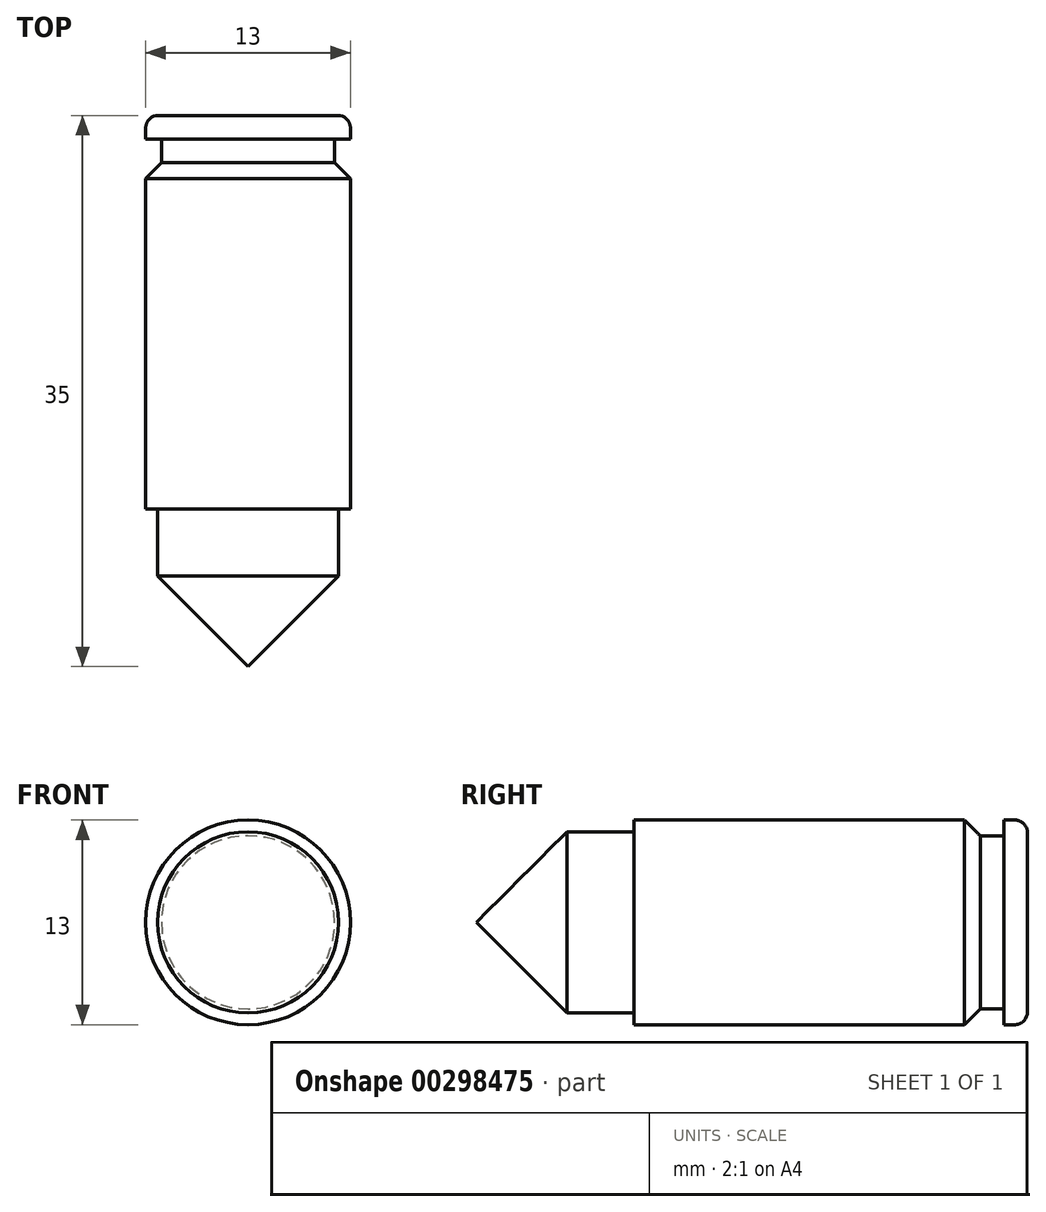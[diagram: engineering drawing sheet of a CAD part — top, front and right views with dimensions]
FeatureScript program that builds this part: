
annotation { "Feature Type Name" : "Feature", "Feature Type Description" : "" }
export const myFeature = defineFeature(function(context is Context, id is Id, definition is map)
    precondition{}
    {
        {
            var Q0;
            Q0=qCreatedBy(makeId("Front.planeOp"),FACE);
            var sketch = newSketch(context, id + "F0", { "sketchPlane" : qUnion([Q0])});
            skCircle(sketch, "E0", {"center": v(0, 0) * mm, "radius": 5.75 * mm});
            skSolve(sketch);
        }
        {
            var Q0;
            Q0 = qSketchRegion(id + "F0", true);
            extrude(context, id + "F1", {"entities" : qUnion([Q0]), "depth" : 10 * mm});
        }
        {
            var Q0;
            Q0=makeQuery(id+"F1.opExtrude","CAP_EDGE",EDGE,{"disambiguationData":[OSD([sQuery(id+"F0.wireOp",EDGE,"E0")])],"isStart":false});
            chamfer(context, id + "F2", {"entities" : qUnion([Q0]), "width" : 5.75 * mm, "tangentPropagation" : true});
        }
        {
            var Q0;
            Q0=makeQuery(id+"F1.opExtrude","CAP_FACE",FACE,{"disambiguationData":[OSD([sQuery(id+"F0.wireOp",EDGE,"E0")])],"isStart":true});
            var sketch = newSketch(context, id + "F3", { "sketchPlane" : qUnion([Q0])});
            skCircle(sketch, "E1", {"center": v(0, 0) * mm, "radius": 6.5 * mm});
            skSolve(sketch);
        }
        {
            var Q0;
            Q0 = qSketchRegion(id + "F3", true);
            extrude(context, id + "F4", {"entities" : qUnion([Q0]), "operationType" : NewBodyOperationType.ADD, "depth" : 22 * mm});
        }
        {
            var Q0;
            Q0=makeQuery(id+"F4.opExtrude","CAP_EDGE",EDGE,{"disambiguationData":[OSD([sQuery(id+"F3.wireOp",EDGE,"E1")])],"isStart":false});
            chamfer(context, id + "F5", {"entities" : qUnion([Q0]), "width" : 1 * mm, "tangentPropagation" : true});
        }
        {
            var Q0;
            Q0=makeQuery(id+"F4.opExtrude","CAP_FACE",FACE,{"disambiguationData":[OSD([sQuery(id+"F3.wireOp",EDGE,"E1")])],"isStart":false});
            var sketch = newSketch(context, id + "F6", { "sketchPlane" : qUnion([Q0])});
            skCircle(sketch, "E2", {"center": v(0, 0) * mm, "radius": 5.5 * mm});
            skSolve(sketch);
        }
        {
            var Q0;
            Q0 = qSketchRegion(id + "F6", true);
            extrude(context, id + "F7", {"entities" : qUnion([Q0]), "operationType" : NewBodyOperationType.ADD, "depth" : 1.5 * mm});
        }
        {
            var Q0;
            Q0=makeQuery(id+"F7.opExtrude","CAP_FACE",FACE,{"disambiguationData":[OSD([sQuery(id+"F6.wireOp",EDGE,"E2")])],"isStart":false});
            var sketch = newSketch(context, id + "F8", { "sketchPlane" : qUnion([Q0])});
            skCircle(sketch, "E3", {"center": v(0, 0) * mm, "radius": 6.5 * mm});
            skSolve(sketch);
        }
        {
            var Q0;
            Q0 = qSketchRegion(id + "F8", true);
            extrude(context, id + "F9", {"entities" : qUnion([Q0]), "operationType" : NewBodyOperationType.ADD, "depth" : 1.5 * mm});
        }
        {
            var Q0;
            Q0=makeQuery(id+"F9.opExtrude","CAP_EDGE",EDGE,{"disambiguationData":[OSD([sQuery(id+"F8.wireOp",EDGE,"E3")])],"isStart":false});
            fillet(context, id + "F10", {"entities" : qUnion([Q0]), "radius" : 0.8 * mm, "tangentPropagation" : true, "allowEdgeOverflow" : false});
        }
    });
